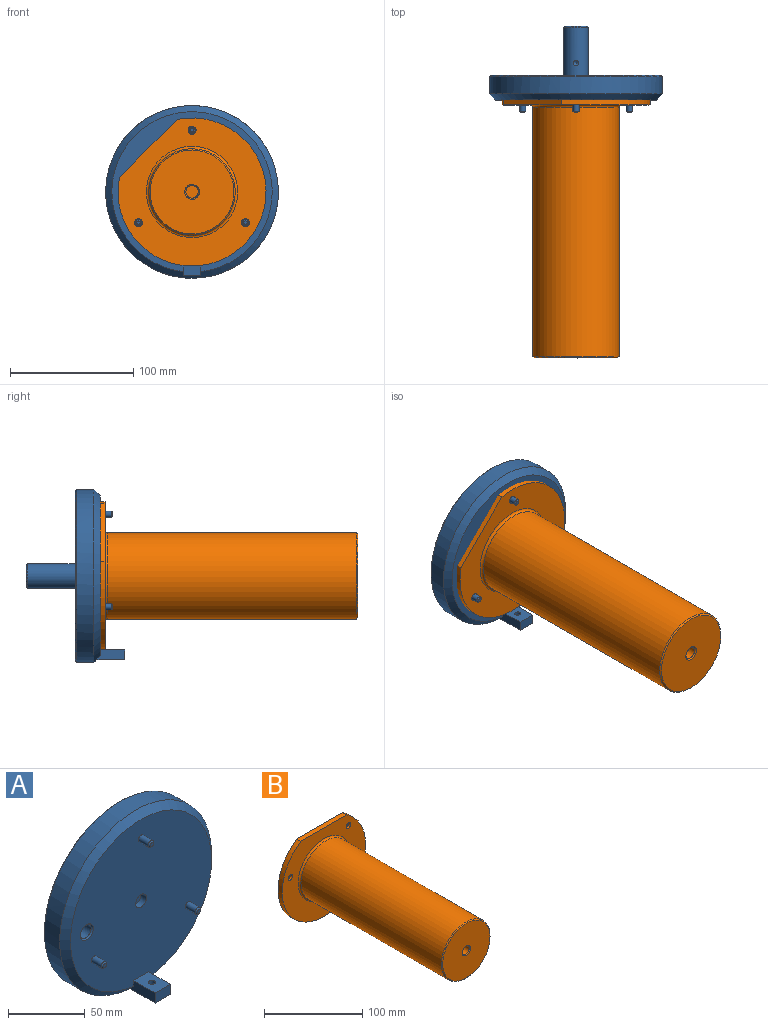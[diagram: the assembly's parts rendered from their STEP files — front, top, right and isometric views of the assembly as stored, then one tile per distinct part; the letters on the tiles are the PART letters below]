
ASSEMBLY  parts=2 mates=1
PART A: 33 faces, bbox 140x80x140 mm
  f0: cylinder r=10mm len=39mm, axis (0,-1,0), area 2434.4mm2, adj f8,f22,f23
  f1: cylinder r=2.5mm len=9mm, axis (0,1,0), area 141.4mm2, adj f5,f25
  f2: plane 3x3mm, normal (0,-1,0), area 7.1mm2, adj f25
  f3: cylinder r=2.5mm len=9mm, axis (0,1,0), area 141.4mm2, adj f5,f26
  f4: plane 3x3mm, normal (0,-1,0), area 7.1mm2, adj f26
  f5: plane 130x129.62mm, normal (0,-1,0), area 12954.4mm2, adj f1,f3,f12,f13,f15,f17,f28,f30
  f6: cylinder r=5mm len=18mm, axis (0,-1,0), area 565.5mm2, adj f27,f28
  f7: cylinder r=70mm len=140mm, axis (0,-1,0), area 6157.5mm2, adj f29,f30
  f8: plane 138x138mm, normal (0,1,0), area 14529.9mm2, adj f0,f27,f29
  f9: cylinder r=5mm len=40mm, axis (0,-1,0), area 1256.6mm2, adj f10,f11
  f10: plane 18x18mm, normal (0,1,0), area 175.9mm2, adj f9,f23
  f11: plane 10x10mm, normal (0,1,0), area 78.5mm2, adj f9
  f12: plane 20x14mm, normal (0,0,1), area 264.1mm2, adj f5,f13,f15,f16,f19
  f13: plane 23.37x8.01mm, normal (-1,0,0), area 165.7mm2, adj f5,f12,f14,f16,f30
  f14: plane 23.36x14mm, normal (0,0,-1), area 295.4mm2, adj f13,f15,f16,f20,f30
  f15: plane 23.37x8.01mm, normal (1,0,0), area 165.7mm2, adj f5,f12,f14,f16,f30
  f16: plane 14x8mm, normal (0,-1,0), area 112mm2, adj f12,f13,f14,f15
  f17: cylinder r=2.5mm len=9mm, axis (0,1,0), area 141.4mm2, adj f5,f24
  f18: plane 3x3mm, normal (0,-1,0), area 7.1mm2, adj f24
  f19: cylinder r=2.25mm len=7.25mm, axis (0,0,-1), area 102.5mm2, adj f12,f20
  f20: cone r=2.25mm half-angle=45deg, axis (0,0,-1), area 17.5mm2, adj f14,f19
  f21: cone r=0mm half-angle=59deg, axis (0,0,1), area 18.6mm2, adj f22
  f22: cylinder r=2.25mm len=4.5mm, axis (0,0,1), area 26.5mm2, adj f0,f21
  f23: cone r=10mm half-angle=45deg, axis (0,-1,0), area 84.4mm2, adj f0,f10
  f24: cone r=1.5mm half-angle=45deg, axis (0,1,0), area 17.8mm2, adj f17,f18
  f25: cone r=1.5mm half-angle=45deg, axis (0,1,0), area 17.8mm2, adj f1,f2
  f26: cone r=1.5mm half-angle=45deg, axis (0,1,0), area 17.8mm2, adj f3,f4
  f27: cone r=6mm half-angle=45deg, axis (0,1,0), area 48.9mm2, adj f6,f8
  f28: cone r=5mm half-angle=45deg, axis (0,-1,0), area 48.9mm2, adj f5,f6
  f29: cone r=70mm half-angle=45deg, axis (0,-1,0), area 617.6mm2, adj f7,f8
  f30: cone r=65mm half-angle=45deg, axis (0,1,0), area 2937mm2, adj f5,f7,f13,f14,f15
  f31: cylinder r=5mm len=10mm, axis (0,-1,0), area 157.1mm2, adj f5,f32
  f32: plane 10x10mm, normal (0,-1,0), area 78.5mm2, adj f31
PART B: 35 faces, bbox 120x215x110 mm
  f0: cylinder r=1.7mm len=3.4mm, axis (0,-1,0), area 21.4mm2, adj f14,f17
  f1: plane 6.5x6.5mm, normal (0,-1,0), area 18mm2, adj f2,f14
  f2: cylinder r=3.25mm len=6.5mm, axis (0,-1,0), area 61.3mm2, adj f1,f10
  f3: cylinder r=1.7mm len=3.4mm, axis (0,-1,0), area 21.4mm2, adj f15,f18
  f4: plane 6.5x6.5mm, normal (0,-1,0), area 18mm2, adj f5,f15
  f5: cylinder r=3.25mm len=6.5mm, axis (0,-1,0), area 61.3mm2, adj f4,f10
  f6: plane 66.33x6mm, normal (0,0,1), area 398mm2, adj f7,f9,f10
  f7: cylinder r=60mm len=120mm, axis (0,-1,0), area 1840.3mm2, adj f6,f9,f10
  f8: cylinder r=30mm len=204mm, axis (0,-1,0), area 38453.1mm2, adj f9,f28
  f9: plane 120x110mm, normal (0,1,0), area 7986.5mm2, adj f6,f7,f8,f17,f18,f19
  f10: plane 120x110mm, normal (0,-1,0), area 6459.2mm2, adj f2,f5,f6,f7,f13,f27
  f11: cylinder r=1.7mm len=3.4mm, axis (0,-1,0), area 21.4mm2, adj f16,f19
  f12: plane 6.5x6.5mm, normal (0,-1,0), area 18mm2, adj f13,f16
  f13: cylinder r=3.25mm len=6.5mm, axis (0,-1,0), area 61.3mm2, adj f10,f12
  f14: cone r=1.7mm half-angle=45deg, axis (0,-1,0), area 8.7mm2, adj f0,f1
  f15: cone r=1.7mm half-angle=45deg, axis (0,-1,0), area 8.7mm2, adj f3,f4
  f16: cone r=1.7mm half-angle=45deg, axis (0,-1,0), area 8.7mm2, adj f11,f12
  f17: cone r=1.7mm half-angle=45deg, axis (0,1,0), area 8.7mm2, adj f0,f9
  f18: cone r=1.7mm half-angle=45deg, axis (0,1,0), area 8.7mm2, adj f3,f9
  f19: cone r=1.7mm half-angle=45deg, axis (0,1,0), area 8.7mm2, adj f9,f11
  f20: cylinder r=35mm len=202mm, axis (0,1,0), area 44422.1mm2, adj f27,f34
  f21: plane 56x56mm, normal (0,1,0), area 2309.1mm2, adj f24,f28
  f22: cylinder r=5mm len=199mm, axis (0,1,0), area 6251.8mm2, adj f26,f29
  f23: plane 68x68mm, normal (0,-1,0), area 3518.6mm2, adj f29,f34
  f24: cylinder r=7mm len=199mm, axis (0,1,0), area 8752.5mm2, adj f21,f30
  f25: plane 12x12mm, normal (0,1,0), area 34.6mm2, adj f30,f31
  f26: plane 10x10mm, normal (0,-1,0), area 78.5mm2, adj f22
  f27: torus R=37mm, axis (0,-1,0), area 705.2mm2, adj f10,f20
  f28: torus R=28mm, axis (0,-1,0), area 577.8mm2, adj f8,f21
  f29: cone r=5mm half-angle=45deg, axis (0,-1,0), area 48.9mm2, adj f22,f23
  f30: cone r=7mm half-angle=45deg, axis (0,-1,0), area 57.8mm2, adj f24,f25
  f31: cylinder r=5mm len=10mm, axis (0,-1,0), area 282.7mm2, adj f25,f33
  f32: plane 8x8mm, normal (0,1,0), area 50.3mm2, adj f33
  f33: cone r=5mm half-angle=45deg, axis (0,-1,0), area 40mm2, adj f31,f32
  f34: cone r=34mm half-angle=45deg, axis (0,1,0), area 306.6mm2, adj f20,f23
PLACE A rot(axis=(-0.04,0.73,0.68),0deg) t=(-16.56,-33.39,58.42)mm fixed
PLACE B rot(axis=(0,-1,0),45deg) t=(-16.56,-37.39,58.42)mm
MATE cylindrical B.f31 <-> A.f9  axis (0,-1,0) through (-16.56,-28.39,58.42)mm
